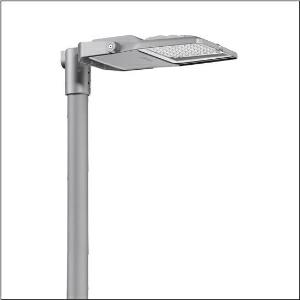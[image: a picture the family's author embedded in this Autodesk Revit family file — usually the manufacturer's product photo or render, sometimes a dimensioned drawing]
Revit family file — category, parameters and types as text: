
# Revit family: floodlight_fl_21_mini___pl64_5xa7776c2e3a_3ffb
name_source: partatom
category: Lighting Fixtures
units: mm (PartAtom-declared; Revit-internal decimal feet)

## family parameters
Cut with Voids When Loaded = No
Host = Face
Light Source = No
Part Type = Normal
Room Calculation Point = No
Round Connector Dimension = Use Diameter
Shared = No

## types (1)
- --- (1 x LED, 11770 lm, 89 W, 3000K)
    Apparent Load = 89 VA
    CIE Flux Codes = 28 80 98 100 100
    Color Rendering = 70
    Color Temperature = 3000K
    Default Elevation = 1800 mm
    Description = Floodlight FL 21 mini, floodlight, primary light control with lens, of PMMA, primary optical cover: protective disc, of toughened safety glass, transparent, light distribution: PL64, light emission: direct distribution, installation type: surface-mounted, LED, High Power LED, rated luminous flux: 11.770lm, luminous efficacy: 132lm/W, light colour: 730, colour temperature: 3000K, control: flexible luminous flux parameterisation, time-dependent luminous flux control, constant luminous flux control, overheat protection, presetting dimming logarithmic, with terminal, 6-pole, mains connection: 220..240V, AC, 50/60Hz, start of lifetime: 89W, end of service life: 94W, reduction: 43W, luminaire housing, of diecast aluminium, powder-coated, Siteco® metallic grey (DB 702S), corrosivity category C5 mid according to DIN EN ISO 12944, sealing non-destructively replaceable, please order mast flange separately, mast bracket, of steel, galvanised, powder-coated, Siteco® metallic grey (DB 702S), Smart Interface below and above, protection rating (complete): IP66, insulation class (complete): insulation class II (safety insulation), certification: CE, ENEC, VDE, protection symbol: D, impact resistance: IK08, permissible operating ambient temperature: -40..+40°C, permissible operating ambient temperature for outdoor applications: -40..+50°C, standard: DIN EN 12944, LABS conformity tested according to VDMA 24364:2018-05, packaging unit: 1 piece

Light Distribution: PL64
    Height = 70 mm
    Lamp = 1 x LED
    Lamp Light Flux = 11770 lm
    Lamp Power = 89 W
    Lamp count = 1
    Length = 485 mm
    Luminous efficacy = 132 lm/W
    Manufacturer = Siteco
    ModVariant = No
    Model = 5XA7776C2E3A
    Number of Poles = 1
    OnlyDefault = Yes
    Power Factor = 1
    Product Name = Floodlight FL 21 mini | PL64
    Product group = floodlight | pylon annexe
    ProductGroupID = 6200
    Protection Class = Protection class II
    Protection Degree = IP 66
    RLX_Detail_Level = 1
    RLX_Emergency_Light_Flux = 0 lm
    RLX_Emergency_Type = 0
    RLX_Emergency_Type_DB = No
    RlxData = <blob elided: 100917 chars, md5=bd0fb299>
    Socket = socket
    Standby Power = 0 W
    System Light Flux = 11770 lm
    System Power = 89 W
    Type Comments = factory setting: luminous flux: 100 % | dim-lin: 254 | 456 mA
    Type Image = l_1007125.jpg
    URL = http://relux.com
    VarID = @adj_115499
    Voltage = 0 V
    Weight = 0.00 kg
    Width = 337 mm

## geometry (parser evidence)
native form markers: Blend x4, Sweep x11
no freeform markers — native parametric forms only
